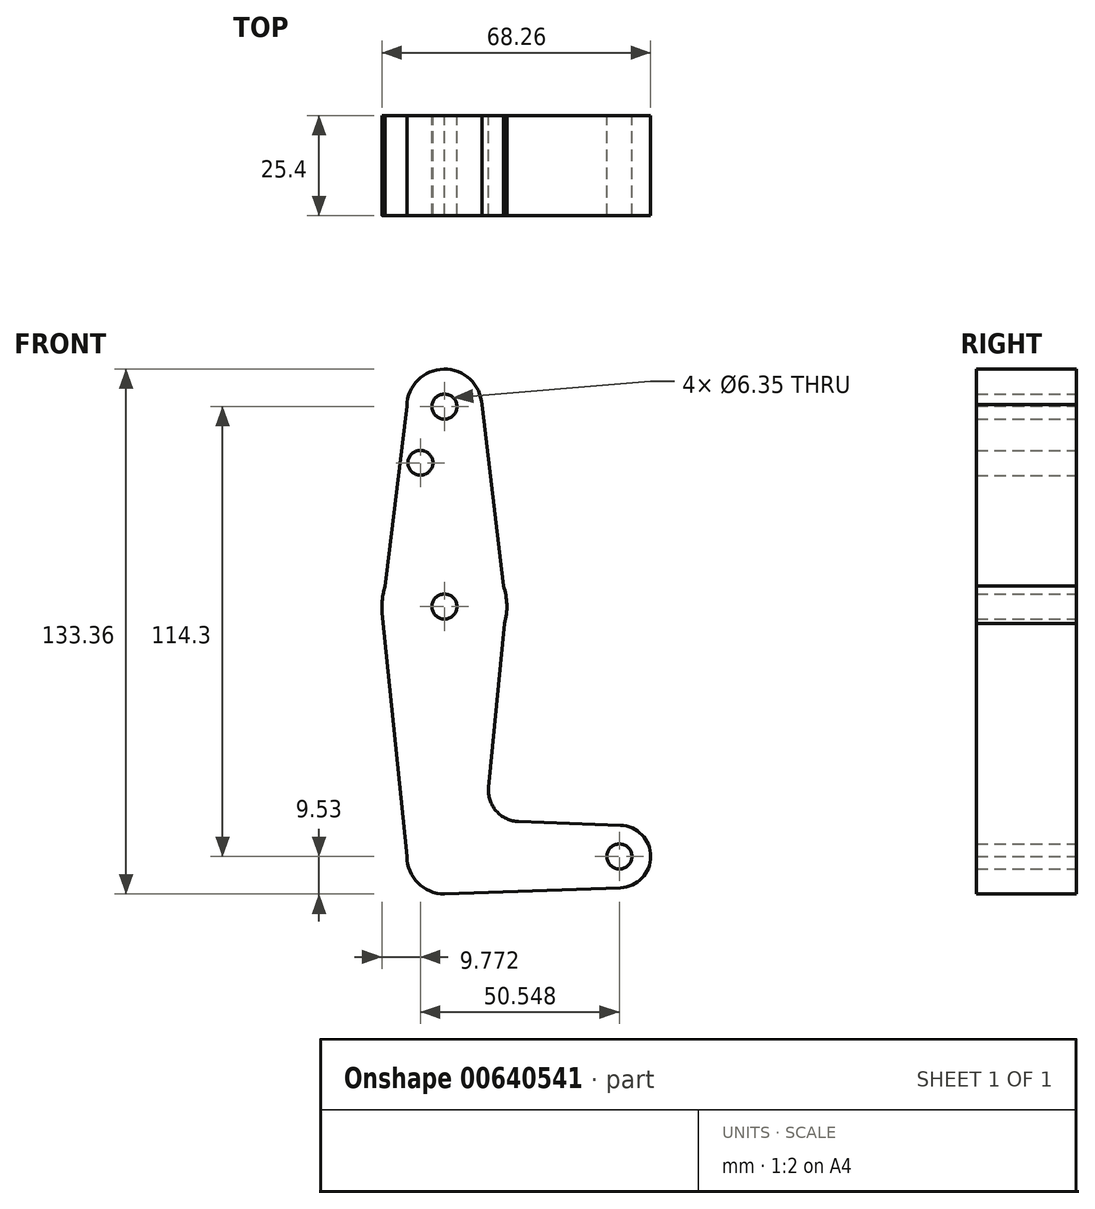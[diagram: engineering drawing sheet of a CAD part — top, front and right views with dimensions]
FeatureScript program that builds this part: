
annotation { "Feature Type Name" : "Feature", "Feature Type Description" : "" }
export const myFeature = defineFeature(function(context is Context, id is Id, definition is map)
    precondition{}
    {
        {
            var Q0;
            Q0=qCreatedBy(makeId("Front.planeOp"),FACE);
            var sketch = newSketch(context, id + "F0", { "sketchPlane" : qUnion([Q0])});
            skLineSegment(sketch, "E0", {"start": v(0, 0) * mm, "end": v(0, 114.3) * mm, "construction": true});
            skLineSegment(sketch, "E1", {"start": v(0, 0) * mm, "end": v(44.45, 0) * mm, "construction": true});
            skCircle(sketch, "E2", {"center": v(0, 114.3) * mm, "radius": 9.53 * mm});
            skCircle(sketch, "E3", {"center": v(0, 63.5) * mm, "radius": 15.88 * mm});
            skCircle(sketch, "E4", {"center": v(0, 0) * mm, "radius": 9.53 * mm});
            skCircle(sketch, "E5", {"center": v(44.45, 0) * mm, "radius": 7.94 * mm});
            skLineSegment(sketch, "E6", {"start": v(-9.52, 114.44) * mm, "end": v(-15.05, 68.56) * mm});
            skLineSegment(sketch, "E7", {"start": v(9.51, 114.76) * mm, "end": v(14.99, 68.73) * mm});
            skLineSegment(sketch, "E8", {"start": v(15.28, 59.2) * mm, "end": v(11.23, 17.57) * mm});
            skLineSegment(sketch, "E9", {"start": v(-9.53, 0) * mm, "end": v(-15.8, 61.9) * mm});
            skLineSegment(sketch, "E10", {"start": v(0, 9.53) * mm, "end": v(0.68, 9.5) * mm});
            skLineSegment(sketch, "E11", {"start": v(0, -9.53) * mm, "end": v(44.73, -7.93) * mm});
            skLineSegment(sketch, "E12.trimOffspring", {"start": v(18.86, 8.85) * mm, "end": v(44.73, 7.93) * mm});
            skPoint(sketch, "E13.visualSharp", {"position": v(10.42, 9.15) * mm});
            skArc(sketch, "E13.filletArc", {"start": v(11.23, 17.57) * mm, "mid": v(13.17, 11.56) * mm, "end": v(18.86, 8.85) * mm});
            skCircle(sketch, "E14", {"center": v(-6.1, 100.03) * mm, "radius": 3.18 * mm});
            skCircle(sketch, "E15", {"center": v(0, 114.3) * mm, "radius": 3.18 * mm});
            skCircle(sketch, "E16", {"center": v(0, 63.5) * mm, "radius": 3.18 * mm});
            skCircle(sketch, "E17", {"center": v(44.45, 0) * mm, "radius": 3.18 * mm});
            skSolve(sketch);
        }
        {
            var Q0;
            Q0=makeQuery(id+"F0.imprint","IMPRINT",FACE,{"disambiguationData":[TD([[makeQuery(id+"F0.imprint","IMPRINT",EDGE,{"derivedFrom":sQuery(id+"F0.wireOp",EDGE,"E15")}),-1.0]])]});
            var Q1;
            Q1=makeQuery(id+"F0.imprint","IMPRINT",FACE,{"disambiguationData":[TD([[makeQuery(id+"F0.imprint","IMPRINT",EDGE,{"derivedFrom":sQuery(id+"F0.wireOp",EDGE,"E17")}),-1.0]])]});
            var Q2;
            Q2=makeQuery(id+"F0.imprint","IMPRINT",FACE,{"disambiguationData":[TD([[makeQuery(id+"F0.imprint","IMPRINT",EDGE,{"derivedFrom":sQuery(id+"F0.wireOp",EDGE,"E16")}),-1.0]])]});
            var Q3;
            {var subQ7=sQuery(id+"F0.wireOp",EDGE,"E8");Q3=makeQuery(id+"F0.imprint","IMPRINT",FACE,{"disambiguationData":[TD([[makeQuery(id+"F0.imprint","IMPRINT",EDGE,{"derivedFrom":subQ7}),-1.0]])]});}
            var Q4;
            {var subQ0=sQuery(id+"F0.wireOp",EDGE,"E10");Q4=makeQuery(id+"F0.imprint","IMPRINT",FACE,{"disambiguationData":[TD([[makeQuery(id+"F0.imprint","IMPRINT",EDGE,{"derivedFrom":subQ0}),-1.0]])]});}
            var Q5;
            {var subQ0=sQuery(id+"F0.wireOp",EDGE,"E11");var subQ1=sQuery(id+"F0.wireOp",EDGE,"E4");var subQ2=makeQuery(id+"F0.imprint","INTERSECT",VERTEX,{"disambiguationData":[OD(0.0)],"derivedFrom":[subQ1,subQ0]});Q5=makeQuery(id+"F0.imprint","IMPRINT",FACE,{"disambiguationData":[TD([[makeQuery(id+"F0.imprint","IMPRINT",EDGE,{"disambiguationData":[TD([[subQ2,-1.0]])],"derivedFrom":subQ1}),1.0]])]});}
            var Q6;
            {var subQ0=sQuery(id+"F0.wireOp",EDGE,"E10");Q6=makeQuery(id+"F0.imprint","IMPRINT",FACE,{"disambiguationData":[TD([[makeQuery(id+"F0.imprint","IMPRINT",EDGE,{"derivedFrom":subQ0}),1.0]])]});}
            var Q7;
            {var subQ1=sQuery(id+"F0.wireOp",EDGE,"E6");Q7=makeQuery(id+"F0.imprint","IMPRINT",FACE,{"disambiguationData":[TD([[makeQuery(id+"F0.imprint","IMPRINT",EDGE,{"derivedFrom":subQ1}),1.0]])]});}
            extrude(context, id + "F1", {"entities" : qUnion([Q0, Q1, Q2, Q3, Q4, Q5, Q6, Q7]), "depth" : 25.4 * mm, "offsetDistance" : 25.4 * mm});
        }
    });
